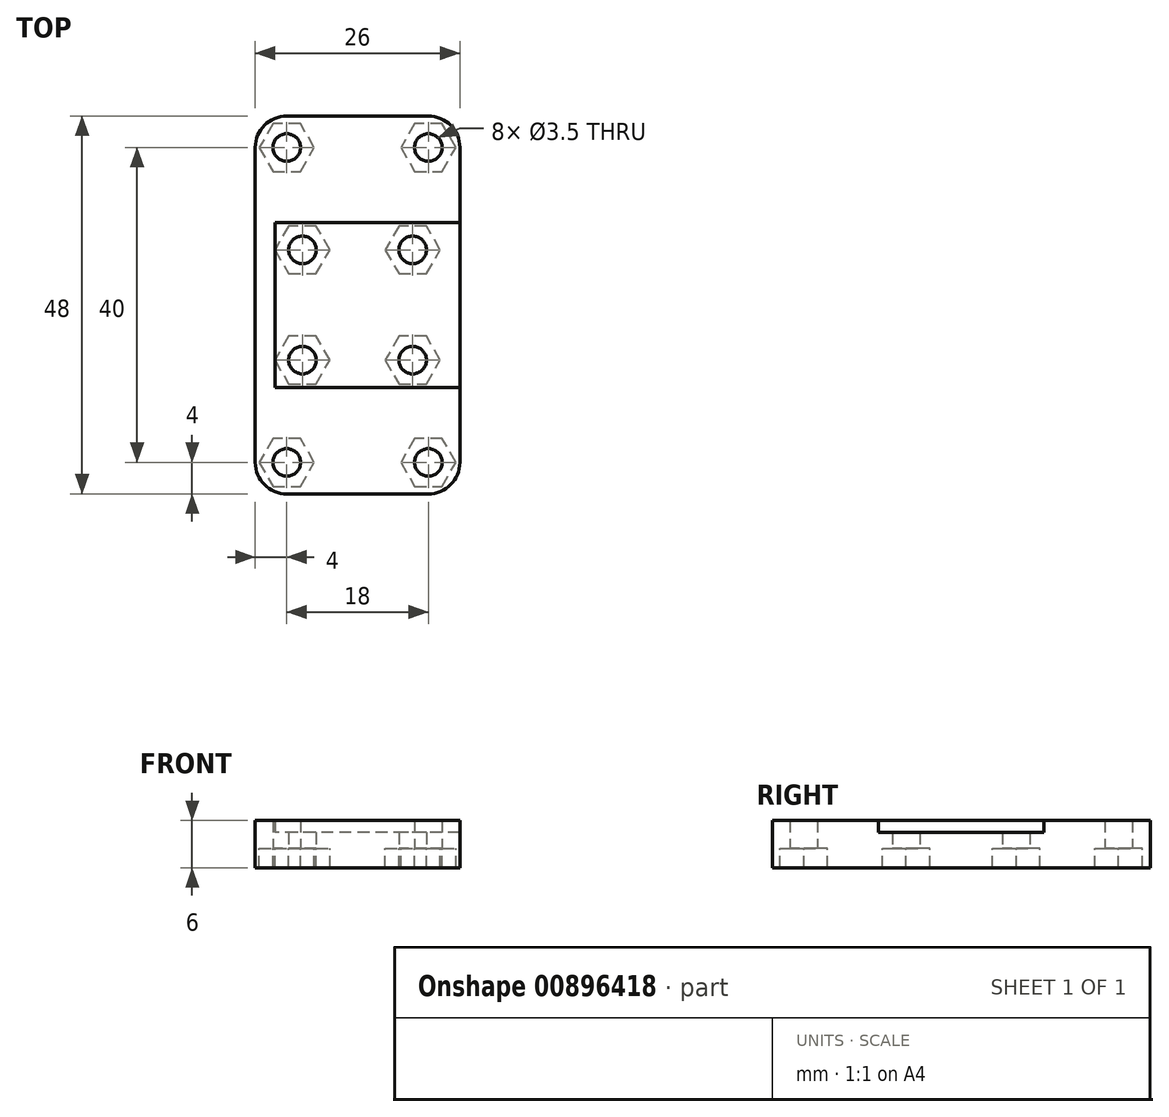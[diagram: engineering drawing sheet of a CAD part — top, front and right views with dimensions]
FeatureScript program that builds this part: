
annotation { "Feature Type Name" : "Feature", "Feature Type Description" : "" }
export const myFeature = defineFeature(function(context is Context, id is Id, definition is map)
    precondition{}
    {
        {
            var Q0;
            Q0=qCreatedBy(makeId("Top.planeOp"),FACE);
            var sketch = newSketch(context, id + "F0", { "sketchPlane" : qUnion([Q0])});
            skPoint(sketch, "E0.middle", {"position": v(0, 0) * mm});
            skCircle(sketch, "E1", {"center": v(-7, 7) * mm, "radius": 1.75 * mm});
            skCircle(sketch, "E2", {"center": v(7, 7) * mm, "radius": 1.75 * mm});
            skCircle(sketch, "E3", {"center": v(7, -7) * mm, "radius": 1.75 * mm});
            skCircle(sketch, "E4", {"center": v(-7, -7) * mm, "radius": 1.75 * mm});
            skCircle(sketch, "E5", {"center": v(-9, 20) * mm, "radius": 1.75 * mm});
            skCircle(sketch, "E6", {"center": v(9, 20) * mm, "radius": 1.75 * mm});
            skCircle(sketch, "E7", {"center": v(9, -20) * mm, "radius": 1.75 * mm});
            skCircle(sketch, "E8", {"center": v(-9, -20) * mm, "radius": 1.75 * mm});
            skCircle(sketch, "E9", {"center": v(-9, -20) * mm, "radius": 4 * mm});
            skCircle(sketch, "E10", {"center": v(9, -20) * mm, "radius": 4 * mm});
            skCircle(sketch, "E11", {"center": v(9, 20) * mm, "radius": 4 * mm});
            skCircle(sketch, "E12", {"center": v(-9, 20) * mm, "radius": 4 * mm});
            skArc(sketch, "E13", {"start": v(-13, -20) * mm, "mid": v(-11.83, -22.83) * mm, "end": v(-9, -24) * mm});
            skArc(sketch, "E14", {"start": v(9, -24) * mm, "mid": v(11.83, -22.83) * mm, "end": v(13, -20) * mm});
            skArc(sketch, "E15", {"start": v(13, 20) * mm, "mid": v(11.83, 22.83) * mm, "end": v(9, 24) * mm});
            skArc(sketch, "E16", {"start": v(-9, 24) * mm, "mid": v(-11.83, 22.83) * mm, "end": v(-13, 20) * mm});
            skLineSegment(sketch, "E17", {"start": v(-13, 20) * mm, "end": v(-13, -20) * mm});
            skLineSegment(sketch, "E18", {"start": v(-9, -24) * mm, "end": v(9, -24) * mm});
            skLineSegment(sketch, "E19", {"start": v(13, -20) * mm, "end": v(13, 20) * mm});
            skLineSegment(sketch, "E20", {"start": v(9, 24) * mm, "end": v(-9, 24) * mm});
            skSolve(sketch);
        }
        {
            var Q0;
            Q0 = qSketchRegion(id + "F0", true);
            extrude(context, id + "F1", {"entities" : qUnion([Q0]), "depth" : 2 * mm, "offsetDistance" : 25 * mm});
        }
        {
            var Q0;
            Q0=makeQuery(id+"F1.opExtrude","CAP_FACE",FACE,{"disambiguationData":[OSD([sQuery(id+"F0.wireOp",EDGE,"E1"),sQuery(id+"F0.wireOp",EDGE,"E2"),sQuery(id+"F0.wireOp",EDGE,"E3"),sQuery(id+"F0.wireOp",EDGE,"E4"),sQuery(id+"F0.wireOp",EDGE,"E5"),sQuery(id+"F0.wireOp",EDGE,"E6"),sQuery(id+"F0.wireOp",EDGE,"E7"),sQuery(id+"F0.wireOp",EDGE,"E8"),sQuery(id+"F0.wireOp",EDGE,"E9"),sQuery(id+"F0.wireOp",EDGE,"E10"),sQuery(id+"F0.wireOp",EDGE,"E11"),sQuery(id+"F0.wireOp",EDGE,"E12"),sQuery(id+"F0.wireOp",EDGE,"E17"),sQuery(id+"F0.wireOp",EDGE,"E18"),sQuery(id+"F0.wireOp",EDGE,"E19"),sQuery(id+"F0.wireOp",EDGE,"E20")])],"isStart":true});
            var sketch = newSketch(context, id + "F2", { "sketchPlane" : qUnion([Q0])});
            skCircle(sketch, "E21.cCircle", {"center": v(-7, 7) * mm, "radius": 3.5 * mm, "construction": true});
            skLineSegment(sketch, "E21.0", {"start": v(-5.25, 10.03) * mm, "end": v(-3.5, 7) * mm});
            skLineSegment(sketch, "E21.1", {"start": v(-3.5, 7) * mm, "end": v(-5.25, 3.97) * mm});
            skLineSegment(sketch, "E21.2", {"start": v(-5.25, 3.97) * mm, "end": v(-8.75, 3.97) * mm});
            skLineSegment(sketch, "E21.3", {"start": v(-8.75, 3.97) * mm, "end": v(-10.5, 7) * mm});
            skLineSegment(sketch, "E21.4", {"start": v(-10.5, 7) * mm, "end": v(-8.75, 10.03) * mm});
            skLineSegment(sketch, "E21.5", {"start": v(-8.75, 10.03) * mm, "end": v(-5.25, 10.03) * mm});
            skCircle(sketch, "E22.cCircle", {"center": v(7, 7) * mm, "radius": 3.5 * mm, "construction": true});
            skLineSegment(sketch, "E22.0", {"start": v(10.5, 7) * mm, "end": v(8.75, 3.97) * mm});
            skLineSegment(sketch, "E22.1", {"start": v(8.75, 3.97) * mm, "end": v(5.25, 3.97) * mm});
            skLineSegment(sketch, "E22.2", {"start": v(5.25, 3.97) * mm, "end": v(3.5, 7) * mm});
            skLineSegment(sketch, "E22.3", {"start": v(3.5, 7) * mm, "end": v(5.25, 10.03) * mm});
            skLineSegment(sketch, "E22.4", {"start": v(5.25, 10.03) * mm, "end": v(8.75, 10.03) * mm});
            skLineSegment(sketch, "E22.5", {"start": v(8.75, 10.03) * mm, "end": v(10.5, 7) * mm});
            skCircle(sketch, "E23.cCircle", {"center": v(7, -7) * mm, "radius": 3.5 * mm, "construction": true});
            skLineSegment(sketch, "E23.0", {"start": v(10.5, -7) * mm, "end": v(8.75, -10.03) * mm});
            skLineSegment(sketch, "E23.1", {"start": v(8.75, -10.03) * mm, "end": v(5.25, -10.03) * mm});
            skLineSegment(sketch, "E23.2", {"start": v(5.25, -10.03) * mm, "end": v(3.5, -7) * mm});
            skLineSegment(sketch, "E23.3", {"start": v(3.5, -7) * mm, "end": v(5.25, -3.97) * mm});
            skLineSegment(sketch, "E23.4", {"start": v(5.25, -3.97) * mm, "end": v(8.75, -3.97) * mm});
            skLineSegment(sketch, "E23.5", {"start": v(8.75, -3.97) * mm, "end": v(10.5, -7) * mm});
            skCircle(sketch, "E24.cCircle", {"center": v(-7, -7) * mm, "radius": 3.5 * mm, "construction": true});
            skLineSegment(sketch, "E24.0", {"start": v(-3.5, -7) * mm, "end": v(-5.25, -10.03) * mm});
            skLineSegment(sketch, "E24.1", {"start": v(-5.25, -10.03) * mm, "end": v(-8.75, -10.03) * mm});
            skLineSegment(sketch, "E24.2", {"start": v(-8.75, -10.03) * mm, "end": v(-10.5, -7) * mm});
            skLineSegment(sketch, "E24.3", {"start": v(-10.5, -7) * mm, "end": v(-8.75, -3.97) * mm});
            skLineSegment(sketch, "E24.4", {"start": v(-8.75, -3.97) * mm, "end": v(-5.25, -3.97) * mm});
            skLineSegment(sketch, "E24.5", {"start": v(-5.25, -3.97) * mm, "end": v(-3.5, -7) * mm});
            skCircle(sketch, "E25.cCircle", {"center": v(-9, 20) * mm, "radius": 3.5 * mm, "construction": true});
            skLineSegment(sketch, "E25.0", {"start": v(-5.5, 20) * mm, "end": v(-7.25, 16.97) * mm});
            skLineSegment(sketch, "E25.1", {"start": v(-7.25, 16.97) * mm, "end": v(-10.75, 16.97) * mm});
            skLineSegment(sketch, "E25.2", {"start": v(-10.75, 16.97) * mm, "end": v(-12.5, 20) * mm});
            skLineSegment(sketch, "E25.3", {"start": v(-12.5, 20) * mm, "end": v(-10.75, 23.03) * mm});
            skLineSegment(sketch, "E25.4", {"start": v(-10.75, 23.03) * mm, "end": v(-7.25, 23.03) * mm});
            skLineSegment(sketch, "E25.5", {"start": v(-7.25, 23.03) * mm, "end": v(-5.5, 20) * mm});
            skCircle(sketch, "E26.cCircle", {"center": v(9, 20) * mm, "radius": 3.5 * mm, "construction": true});
            skLineSegment(sketch, "E26.0", {"start": v(10.75, 23.03) * mm, "end": v(12.5, 20) * mm});
            skLineSegment(sketch, "E26.1", {"start": v(12.5, 20) * mm, "end": v(10.75, 16.97) * mm});
            skLineSegment(sketch, "E26.2", {"start": v(10.75, 16.97) * mm, "end": v(7.25, 16.97) * mm});
            skLineSegment(sketch, "E26.3", {"start": v(7.25, 16.97) * mm, "end": v(5.5, 20) * mm});
            skLineSegment(sketch, "E26.4", {"start": v(5.5, 20) * mm, "end": v(7.25, 23.03) * mm});
            skLineSegment(sketch, "E26.5", {"start": v(7.25, 23.03) * mm, "end": v(10.75, 23.03) * mm});
            skCircle(sketch, "E27.cCircle", {"center": v(9, -20) * mm, "radius": 3.5 * mm, "construction": true});
            skLineSegment(sketch, "E27.0", {"start": v(12.5, -20) * mm, "end": v(10.75, -23.03) * mm});
            skLineSegment(sketch, "E27.1", {"start": v(10.75, -23.03) * mm, "end": v(7.25, -23.03) * mm});
            skLineSegment(sketch, "E27.2", {"start": v(7.25, -23.03) * mm, "end": v(5.5, -20) * mm});
            skLineSegment(sketch, "E27.3", {"start": v(5.5, -20) * mm, "end": v(7.25, -16.97) * mm});
            skLineSegment(sketch, "E27.4", {"start": v(7.25, -16.97) * mm, "end": v(10.75, -16.97) * mm});
            skLineSegment(sketch, "E27.5", {"start": v(10.75, -16.97) * mm, "end": v(12.5, -20) * mm});
            skCircle(sketch, "E28.cCircle", {"center": v(-9, -20) * mm, "radius": 3.5 * mm, "construction": true});
            skLineSegment(sketch, "E28.0", {"start": v(-5.5, -20) * mm, "end": v(-7.25, -23.03) * mm});
            skLineSegment(sketch, "E28.1", {"start": v(-7.25, -23.03) * mm, "end": v(-10.75, -23.03) * mm});
            skLineSegment(sketch, "E28.2", {"start": v(-10.75, -23.03) * mm, "end": v(-12.5, -20) * mm});
            skLineSegment(sketch, "E28.3", {"start": v(-12.5, -20) * mm, "end": v(-10.75, -16.97) * mm});
            skLineSegment(sketch, "E28.4", {"start": v(-10.75, -16.97) * mm, "end": v(-7.25, -16.97) * mm});
            skLineSegment(sketch, "E28.5", {"start": v(-7.25, -16.97) * mm, "end": v(-5.5, -20) * mm});
            skArc(sketch, "E29", {"start": v(-13, 20) * mm, "mid": v(-11.83, 22.83) * mm, "end": v(-9, 24) * mm});
            skArc(sketch, "E30", {"start": v(9, 24) * mm, "mid": v(11.83, 22.83) * mm, "end": v(13, 20) * mm});
            skArc(sketch, "E31", {"start": v(13, -20) * mm, "mid": v(11.83, -22.83) * mm, "end": v(9, -24) * mm});
            skArc(sketch, "E32", {"start": v(-9, -24) * mm, "mid": v(-11.83, -22.83) * mm, "end": v(-13, -20) * mm});
            skLineSegment(sketch, "E33", {"start": v(-13, -20) * mm, "end": v(-13, 20) * mm});
            skLineSegment(sketch, "E34", {"start": v(-9, 24) * mm, "end": v(9, 24) * mm});
            skLineSegment(sketch, "E35", {"start": v(13, 20) * mm, "end": v(13, -20) * mm});
            skLineSegment(sketch, "E36", {"start": v(9, -24) * mm, "end": v(-9, -24) * mm});
            skSolve(sketch);
        }
        {
            var Q0;
            Q0 = qSketchRegion(id + "F2", true);
            extrude(context, id + "F3", {"entities" : qUnion([Q0]), "operationType" : NewBodyOperationType.ADD, "depth" : 2.5 * mm, "offsetDistance" : 25 * mm});
        }
        {
            var Q0;
            Q0=makeQuery(id+"F1.opExtrude","CAP_FACE",FACE,{"disambiguationData":[OSD([sQuery(id+"F0.wireOp",EDGE,"E1"),sQuery(id+"F0.wireOp",EDGE,"E2"),sQuery(id+"F0.wireOp",EDGE,"E3"),sQuery(id+"F0.wireOp",EDGE,"E4"),sQuery(id+"F0.wireOp",EDGE,"E5"),sQuery(id+"F0.wireOp",EDGE,"E6"),sQuery(id+"F0.wireOp",EDGE,"E7"),sQuery(id+"F0.wireOp",EDGE,"E8"),sQuery(id+"F0.wireOp",EDGE,"E9"),sQuery(id+"F0.wireOp",EDGE,"E10"),sQuery(id+"F0.wireOp",EDGE,"E11"),sQuery(id+"F0.wireOp",EDGE,"E12"),sQuery(id+"F0.wireOp",EDGE,"E17"),sQuery(id+"F0.wireOp",EDGE,"E18"),sQuery(id+"F0.wireOp",EDGE,"E19"),sQuery(id+"F0.wireOp",EDGE,"E20")])],"isStart":false});
            var sketch = newSketch(context, id + "F4", { "sketchPlane" : qUnion([Q0])});
            skLineSegment(sketch, "E37.bottom", {"start": v(10.5, 10.5) * mm, "end": v(-10.5, 10.5) * mm});
            skLineSegment(sketch, "E37.top", {"start": v(10.5, -10.5) * mm, "end": v(-10.5, -10.5) * mm});
            skLineSegment(sketch, "E37.right", {"start": v(-10.5, 10.5) * mm, "end": v(-10.5, -10.5) * mm});
            skPoint(sketch, "E37.middle", {"position": v(0, 0) * mm});
            skArc(sketch, "E38", {"start": v(-13, 20) * mm, "mid": v(-11.83, 22.83) * mm, "end": v(-9, 24) * mm});
            skArc(sketch, "E39", {"start": v(9, 24) * mm, "mid": v(11.83, 22.83) * mm, "end": v(13, 20) * mm});
            skArc(sketch, "E40", {"start": v(13, -20) * mm, "mid": v(11.83, -22.83) * mm, "end": v(9, -24) * mm});
            skArc(sketch, "E41", {"start": v(-9, -24) * mm, "mid": v(-11.83, -22.83) * mm, "end": v(-13, -20) * mm});
            skLineSegment(sketch, "E42", {"start": v(-13, -20) * mm, "end": v(-13, 20) * mm});
            skLineSegment(sketch, "E43", {"start": v(-9, 24) * mm, "end": v(9, 24) * mm});
            skLineSegment(sketch, "E44", {"start": v(10.5, 10.5) * mm, "end": v(13, 10.5) * mm});
            skLineSegment(sketch, "E45", {"start": v(13, 10.5) * mm, "end": v(13, 20) * mm});
            skLineSegment(sketch, "E46", {"start": v(10.5, -10.5) * mm, "end": v(13, -10.5) * mm});
            skLineSegment(sketch, "E47", {"start": v(13, -10.5) * mm, "end": v(13, -20) * mm});
            skLineSegment(sketch, "E48", {"start": v(9, -24) * mm, "end": v(-9, -24) * mm});
            skCircle(sketch, "E49", {"center": v(-9, 20) * mm, "radius": 1.75 * mm});
            skCircle(sketch, "E50", {"center": v(9, 20) * mm, "radius": 1.75 * mm});
            skCircle(sketch, "E51", {"center": v(9, -20) * mm, "radius": 1.75 * mm});
            skCircle(sketch, "E52", {"center": v(-9, -20) * mm, "radius": 1.75 * mm});
            skSolve(sketch);
        }
        {
            var Q0;
            Q0 = qSketchRegion(id + "F4", true);
            extrude(context, id + "F5", {"entities" : qUnion([Q0]), "operationType" : NewBodyOperationType.ADD, "depth" : 1.5 * mm, "offsetDistance" : 25 * mm});
        }
    });
